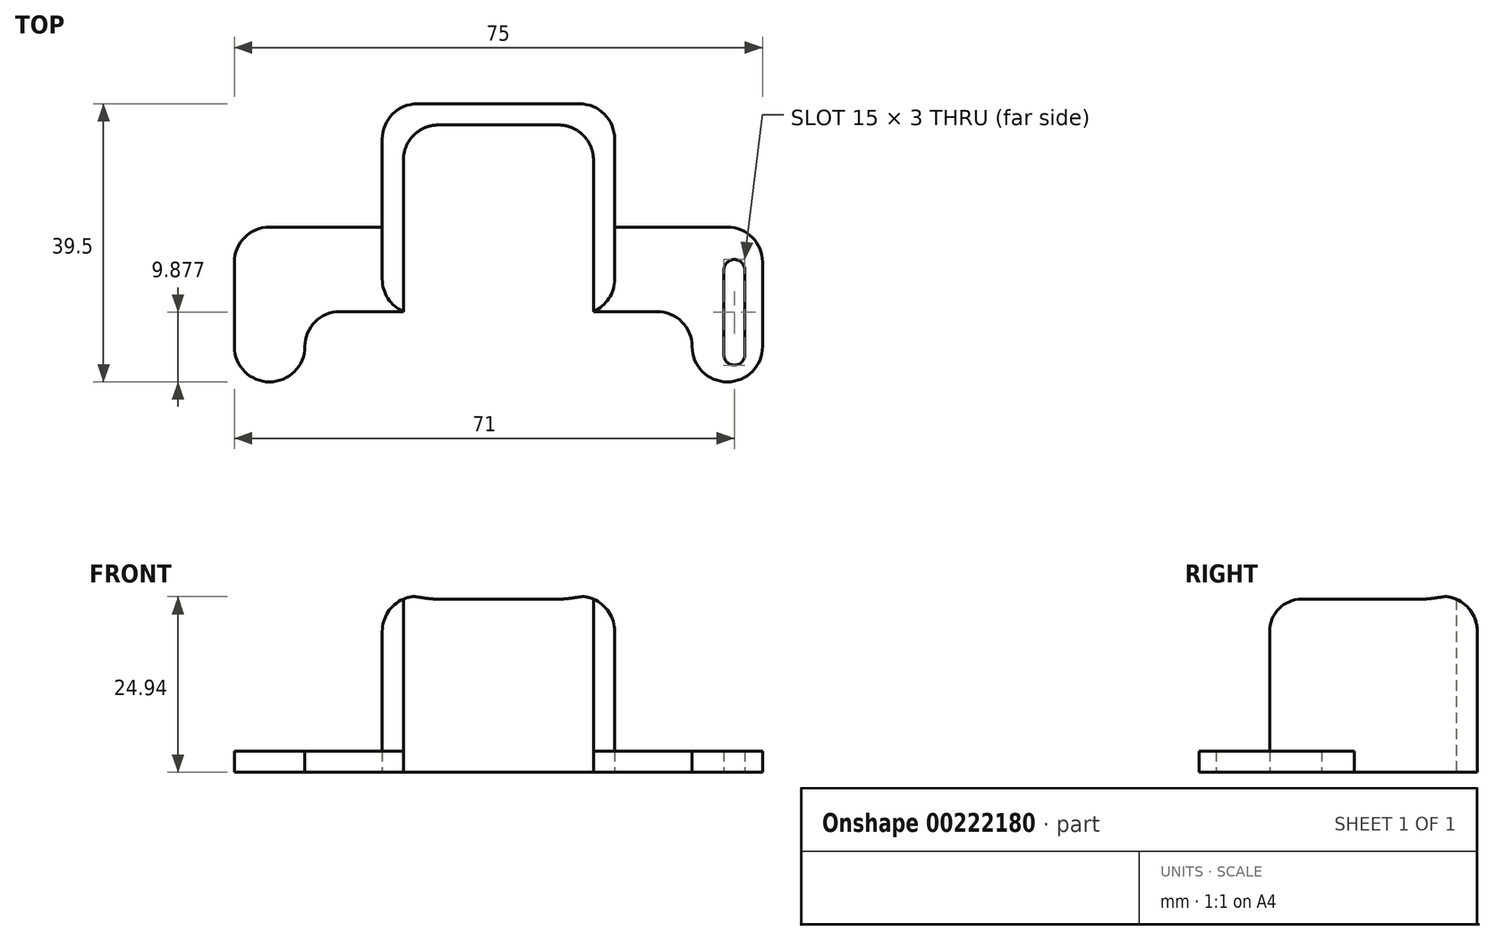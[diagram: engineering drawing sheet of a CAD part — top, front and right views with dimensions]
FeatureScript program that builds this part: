
annotation { "Feature Type Name" : "Feature", "Feature Type Description" : "" }
export const myFeature = defineFeature(function(context is Context, id is Id, definition is map)
    precondition{}
    {
        {
            var Q0;
            Q0=qCreatedBy(makeId("Top.planeOp"),FACE);
            var sketch = newSketch(context, id + "F0", { "sketchPlane" : qUnion([Q0])});
            skLineSegment(sketch, "E0", {"start": v(0, 39.5) * mm, "end": v(16.5, 39.5) * mm});
            skLineSegment(sketch, "E1", {"start": v(16.5, 39.5) * mm, "end": v(16.5, 22) * mm});
            skLineSegment(sketch, "E2", {"start": v(16.5, 22) * mm, "end": v(37.5, 22) * mm});
            skLineSegment(sketch, "E3", {"start": v(37.5, 22) * mm, "end": v(37.5, 0) * mm});
            skLineSegment(sketch, "E4", {"start": v(37.5, 0) * mm, "end": v(27.5, 0) * mm});
            skLineSegment(sketch, "E5", {"start": v(27.5, 0) * mm, "end": v(27.5, 10) * mm});
            skLineSegment(sketch, "E6", {"start": v(27.5, 10) * mm, "end": v(13.5, 10) * mm});
            skLineSegment(sketch, "E7", {"start": v(13.5, 10) * mm, "end": v(13.5, 36.5) * mm});
            skLineSegment(sketch, "E8", {"start": v(13.5, 36.5) * mm, "end": v(0, 36.5) * mm});
            skLineSegment(sketch, "E9.MirrorCS", {"start": v(0, 39.5) * mm, "end": v(-16.5, 39.5) * mm});
            skLineSegment(sketch, "E10.MirrorCS", {"start": v(-13.5, 36.5) * mm, "end": v(0, 36.5) * mm});
            skLineSegment(sketch, "E11.MirrorCS", {"start": v(-16.5, 39.5) * mm, "end": v(-16.5, 22) * mm});
            skLineSegment(sketch, "E12.MirrorCS", {"start": v(-13.5, 10) * mm, "end": v(-13.5, 36.5) * mm});
            skLineSegment(sketch, "E13.MirrorCS", {"start": v(-16.5, 22) * mm, "end": v(-37.5, 22) * mm});
            skLineSegment(sketch, "E14.MirrorCS", {"start": v(-27.5, 10) * mm, "end": v(-13.5, 10) * mm});
            skLineSegment(sketch, "E15.MirrorCS", {"start": v(-37.5, 22) * mm, "end": v(-37.5, 0) * mm});
            skLineSegment(sketch, "E16.MirrorCS", {"start": v(-27.5, 0) * mm, "end": v(-27.5, 10) * mm});
            skLineSegment(sketch, "E17.MirrorCS", {"start": v(-37.5, 0) * mm, "end": v(-27.5, 0) * mm});
            skPoint(sketch, "E18.firstSnap0", {"position": v(-37.5, 11) * mm});
            skLineSegment(sketch, "E19", {"start": v(-16.5, 22) * mm, "end": v(-16.5, 10) * mm});
            skLineSegment(sketch, "E20", {"start": v(16.5, 22) * mm, "end": v(16.5, 10) * mm});
            skLineSegment(sketch, "E21", {"start": v(-16.5, 10) * mm, "end": v(-13.5, 10) * mm});
            skLineSegment(sketch, "E22", {"start": v(13.5, 10) * mm, "end": v(16.5, 10) * mm});
            skSolve(sketch);
        }
        {
            var Q0;
            Q0=qCreatedBy(makeId("Top.planeOp"),FACE);
            var sketch = newSketch(context, id + "F1", { "sketchPlane" : qUnion([Q0])});
            skLineSegment(sketch, "E23", {"start": v(-33.5, 15.88) * mm, "end": v(-33.5, 3.88) * mm});
            skArc(sketch, "E24.0.startCap", {"start": v(-35, 15.88) * mm, "mid": v(-33.5, 17.38) * mm, "end": v(-32, 15.88) * mm});
            skArc(sketch, "E24.0.endCap", {"start": v(-32, 3.88) * mm, "mid": v(-33.5, 2.38) * mm, "end": v(-35, 3.88) * mm});
            skLineSegment(sketch, "E24.0.left", {"start": v(-32, 15.88) * mm, "end": v(-32, 3.88) * mm});
            skLineSegment(sketch, "E24.0.right", {"start": v(-35, 15.88) * mm, "end": v(-35, 3.88) * mm});
            skLineSegment(sketch, "E25.MirrorCS", {"start": v(35, 15.88) * mm, "end": v(35, 3.88) * mm});
            skLineSegment(sketch, "E26.MirrorCS", {"start": v(32, 15.88) * mm, "end": v(32, 3.88) * mm});
            skLineSegment(sketch, "E27.MirrorCS", {"start": v(33.5, 15.88) * mm, "end": v(33.5, 3.88) * mm});
            skArc(sketch, "E28.MirrorCS", {"start": v(35, 15.88) * mm, "mid": v(33.5, 17.38) * mm, "end": v(32, 15.88) * mm});
            skArc(sketch, "E29.MirrorCS", {"start": v(32, 3.88) * mm, "mid": v(33.5, 2.38) * mm, "end": v(35, 3.88) * mm});
            skSolve(sketch);
        }
        {
            var Q0;
            Q0=makeQuery(id+"F0.imprint","IMPRINT",FACE,{"disambiguationData":[TD([[makeQuery(id+"F0.imprint","IMPRINT",EDGE,{"derivedFrom":sQuery(id+"F0.wireOp",EDGE,"E0")}),-1.0]])]});
            var Q1;
            Q1=sQuery(id+"F0.wireOp",EDGE,"E12.MirrorCS");
            var Q2;
            Q2=sQuery(id+"F0.wireOp",EDGE,"E10.MirrorCS");
            var Q3;
            Q3=sQuery(id+"F0.wireOp",EDGE,"E8");
            var Q4;
            Q4=sQuery(id+"F0.wireOp",EDGE,"E7");
            var Q5;
            Q5=sQuery(id+"F0.wireOp",EDGE,"E1");
            var Q6;
            Q6=sQuery(id+"F0.wireOp",EDGE,"E20");
            var Q7;
            Q7=sQuery(id+"F0.wireOp",EDGE,"E0");
            var Q8;
            Q8=sQuery(id+"F0.wireOp",EDGE,"E9.MirrorCS");
            var Q9;
            Q9=sQuery(id+"F0.wireOp",EDGE,"E11.MirrorCS");
            var Q10;
            Q10=sQuery(id+"F0.wireOp",EDGE,"E19");
            var Q11;
            Q11=sQuery(id+"F0.wireOp",EDGE,"E21");
            var Q12;
            Q12=sQuery(id+"F0.wireOp",EDGE,"E22");
            extrude(context, id + "F2", {"entities" : qUnion([Q0]), "surfaceEntities" : qUnion([Q1, Q2, Q3, Q4, Q5, Q6, Q7, Q8, Q9, Q10, Q11, Q12]), "depth" : 25 * mm});
        }
        {
            var Q0;
            Q0=makeQuery(id+"F0.imprint","IMPRINT",FACE,{"disambiguationData":[TD([[makeQuery(id+"F0.imprint","IMPRINT",EDGE,{"derivedFrom":sQuery(id+"F0.wireOp",EDGE,"E13.MirrorCS")}),1.0]])]});
            var Q1;
            Q1=makeQuery(id+"F0.imprint","IMPRINT",FACE,{"disambiguationData":[TD([[makeQuery(id+"F0.imprint","IMPRINT",EDGE,{"derivedFrom":sQuery(id+"F0.wireOp",EDGE,"E2")}),-1.0]])]});
            extrude(context, id + "F3", {"entities" : qUnion([Q0, Q1]), "operationType" : NewBodyOperationType.ADD, "depth" : 3 * mm});
        }
        {
            var Q0;
            Q0=makeQuery(id+"F1.imprint","IMPRINT",FACE,{"disambiguationData":[TD([[makeQuery(id+"F1.imprint","IMPRINT",EDGE,{"derivedFrom":sQuery(id+"F1.wireOp",EDGE,"E25.MirrorCS")}),-1.0]])]});
            var Q1;
            Q1=makeQuery(id+"F1.imprint","IMPRINT",FACE,{"disambiguationData":[TD([[makeQuery(id+"F1.imprint","IMPRINT",EDGE,{"derivedFrom":sQuery(id+"F1.wireOp",EDGE,"E24.0.startCap")}),-1.0]])]});
            extrude(context, id + "F4", {"entities" : qUnion([Q0, Q1]), "operationType" : NewBodyOperationType.REMOVE, "depth" : 25 * mm});
        }
        {
            var Q0;
            Q0=makeQuery(id+"F3.opExtrude","SWEPT_EDGE",EDGE,{"disambiguationData":[OSD([sQuery(id+"F0.wireOp",EDGE,"E15.MirrorCS"),sQuery(id+"F0.wireOp",EDGE,"E17.MirrorCS")])]});
            var Q1;
            Q1=makeQuery(id+"F3.opExtrude","SWEPT_EDGE",EDGE,{"disambiguationData":[OSD([sQuery(id+"F0.wireOp",EDGE,"E16.MirrorCS"),sQuery(id+"F0.wireOp",EDGE,"E17.MirrorCS")])]});
            var Q2;
            Q2=makeQuery(id+"F3.opExtrude","SWEPT_EDGE",EDGE,{"disambiguationData":[OSD([sQuery(id+"F0.wireOp",EDGE,"E13.MirrorCS"),sQuery(id+"F0.wireOp",EDGE,"E15.MirrorCS")])]});
            var Q3;
            Q3=makeQuery(id+"F3.opExtrude","SWEPT_EDGE",EDGE,{"disambiguationData":[OSD([sQuery(id+"F0.wireOp",EDGE,"E2"),sQuery(id+"F0.wireOp",EDGE,"E3")])]});
            var Q4;
            Q4=makeQuery(id+"F3.opExtrude","SWEPT_EDGE",EDGE,{"disambiguationData":[OSD([sQuery(id+"F0.wireOp",EDGE,"E3"),sQuery(id+"F0.wireOp",EDGE,"E4")])]});
            var Q5;
            Q5=makeQuery(id+"F3.opExtrude","SWEPT_EDGE",EDGE,{"disambiguationData":[OSD([sQuery(id+"F0.wireOp",EDGE,"E4"),sQuery(id+"F0.wireOp",EDGE,"E5")])]});
            var Q6;
            Q6=makeQuery(id+"F3.opExtrude","SWEPT_EDGE",EDGE,{"disambiguationData":[OSD([sQuery(id+"F0.wireOp",EDGE,"E5"),sQuery(id+"F0.wireOp",EDGE,"E6")])]});
            var Q7;
            Q7=makeQuery(id+"F3.opExtrude","SWEPT_EDGE",EDGE,{"disambiguationData":[OSD([sQuery(id+"F0.wireOp",EDGE,"E14.MirrorCS"),sQuery(id+"F0.wireOp",EDGE,"E16.MirrorCS")])]});
            fillet(context, id + "F5", {"entities" : qUnion([Q0, Q1, Q2, Q3, Q4, Q5, Q6, Q7]), "radius" : 5 * mm, "tangentPropagation" : true, "allowEdgeOverflow" : false});
        }
        {
            var Q0;
            Q0=makeQuery(id+"F2.opExtrude","SWEPT_EDGE",EDGE,{"disambiguationData":[OSD([sQuery(id+"F0.wireOp",EDGE,"E0"),sQuery(id+"F0.wireOp",EDGE,"E1")])]});
            var Q1;
            Q1=makeQuery(id+"F2.opExtrude","SWEPT_EDGE",EDGE,{"disambiguationData":[OSD([sQuery(id+"F0.wireOp",EDGE,"E9.MirrorCS"),sQuery(id+"F0.wireOp",EDGE,"E11.MirrorCS")])]});
            var Q2;
            Q2=makeQuery(id+"F2.opExtrude","SWEPT_EDGE",EDGE,{"disambiguationData":[OSD([sQuery(id+"F0.wireOp",EDGE,"E14.MirrorCS"),sQuery(id+"F0.wireOp",EDGE,"E19"),sQuery(id+"F0.wireOp",EDGE,"E21")])]});
            var Q3;
            Q3=makeQuery(id+"F2.opExtrude","SWEPT_EDGE",EDGE,{"disambiguationData":[OSD([sQuery(id+"F0.wireOp",EDGE,"E6"),sQuery(id+"F0.wireOp",EDGE,"E20"),sQuery(id+"F0.wireOp",EDGE,"E22")])]});
            var Q4;
            Q4=makeQuery(id+"F2.opExtrude","SWEPT_EDGE",EDGE,{"disambiguationData":[OSD([sQuery(id+"F0.wireOp",EDGE,"E10.MirrorCS"),sQuery(id+"F0.wireOp",EDGE,"E12.MirrorCS")])]});
            var Q5;
            Q5=makeQuery(id+"F2.opExtrude","SWEPT_EDGE",EDGE,{"disambiguationData":[OSD([sQuery(id+"F0.wireOp",EDGE,"E7"),sQuery(id+"F0.wireOp",EDGE,"E8")])]});
            fillet(context, id + "F6", {"entities" : qUnion([Q0, Q1, Q2, Q3, Q4, Q5]), "radius" : 5 * mm, "tangentPropagation" : true, "allowEdgeOverflow" : false});
        }
        {
            var Q0;
            Q0=makeQuery(id+"F2.opExtrude","CAP_EDGE",EDGE,{"disambiguationData":[OSD([sQuery(id+"F0.wireOp",EDGE,"E11.MirrorCS"),sQuery(id+"F0.wireOp",EDGE,"E19")])],"isStart":false});
            fillet(context, id + "F7", {"entities" : qUnion([Q0]), "radius" : 5 * mm, "tangentPropagation" : true, "allowEdgeOverflow" : false});
        }
    });
